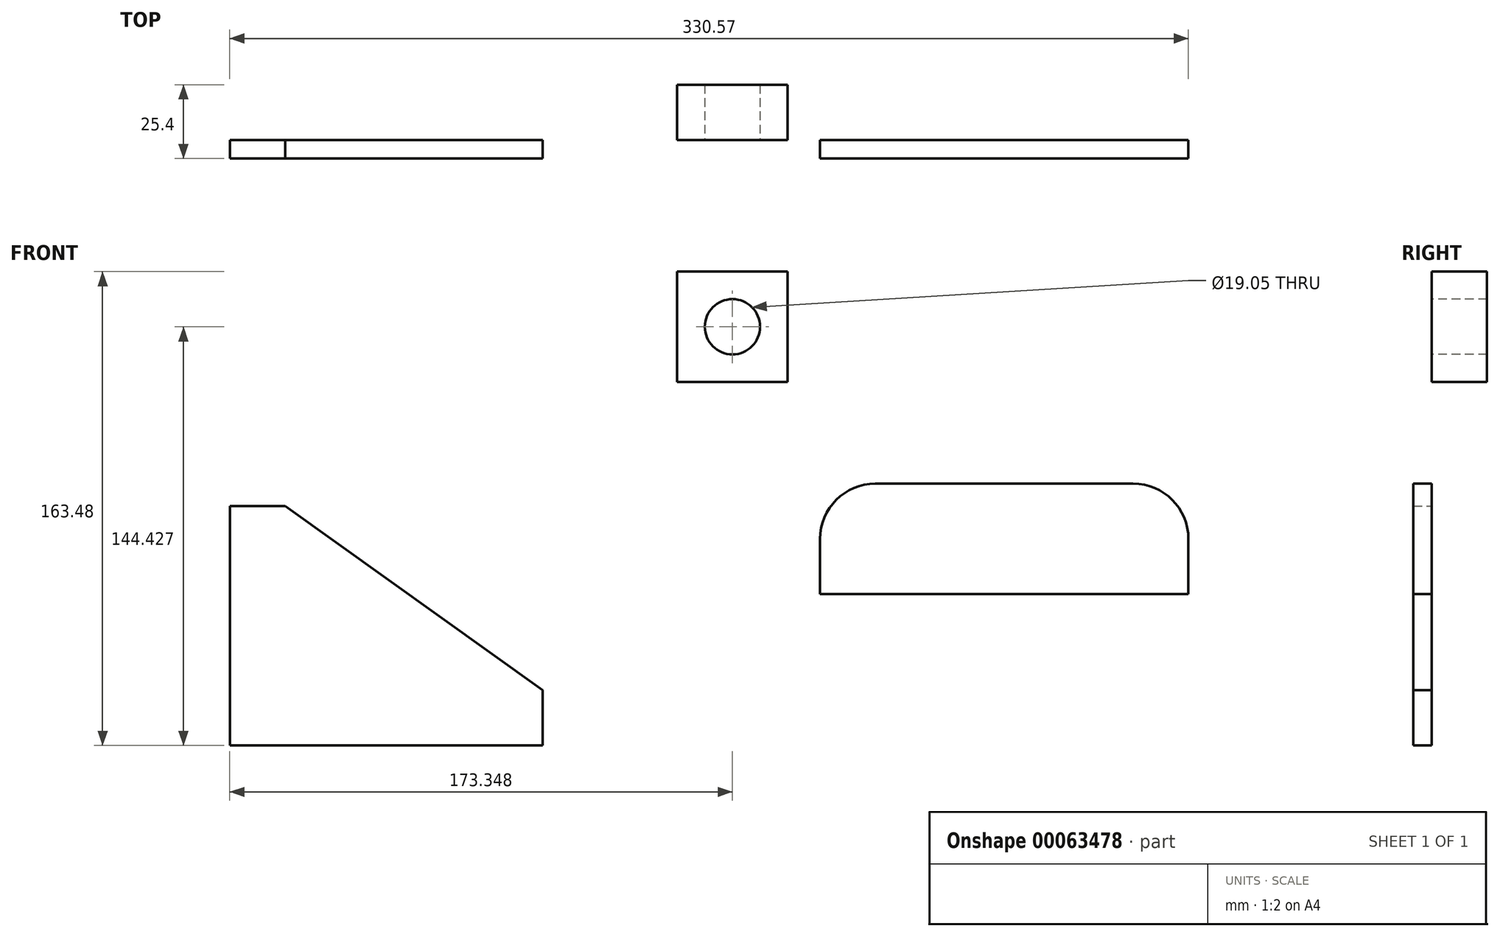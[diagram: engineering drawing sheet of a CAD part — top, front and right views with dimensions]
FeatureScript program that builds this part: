
annotation { "Feature Type Name" : "Feature", "Feature Type Description" : "" }
export const myFeature = defineFeature(function(context is Context, id is Id, definition is map)
    precondition{}
    {
        {
            var Q0;
            Q0=qCreatedBy(makeId("Front.planeOp"),FACE);
            var sketch = newSketch(context, id + "F0", { "sketchPlane" : qUnion([Q0])});
            skLineSegment(sketch, "E0", {"start": v(-40.18, 63.5) * mm, "end": v(-59.23, 63.5) * mm});
            skLineSegment(sketch, "E1", {"start": v(-59.23, 63.5) * mm, "end": v(-59.23, -19.05) * mm});
            skLineSegment(sketch, "E2", {"start": v(-59.23, -19.05) * mm, "end": v(48.72, -19.05) * mm});
            skLineSegment(sketch, "E3", {"start": v(48.72, -19.05) * mm, "end": v(48.72, 0) * mm});
            skLineSegment(sketch, "E4", {"start": v(-40.18, 63.5) * mm, "end": v(48.72, 0) * mm});
            skSolve(sketch);
        }
        {
            var Q0;
            Q0=makeQuery(id+"F0.imprint","IMPRINT",FACE,{"disambiguationData":[TD([[makeQuery(id+"F0.imprint","IMPRINT",EDGE,{"derivedFrom":sQuery(id+"F0.wireOp",EDGE,"E0")}),1.0]])]});
            extrude(context, id + "F1", {"entities" : qUnion([Q0]), "depth" : 6.35 * mm});
        }
        {
            var Q0;
            Q0=qCreatedBy(makeId("Front.planeOp"),FACE);
            var sketch = newSketch(context, id + "F2", { "sketchPlane" : qUnion([Q0])});
            skLineSegment(sketch, "E5.bottom", {"start": v(163.39, 71.27) * mm, "end": v(252.29, 71.27) * mm});
            skLineSegment(sketch, "E5.top", {"start": v(144.34, 33.17) * mm, "end": v(271.34, 33.17) * mm});
            skLineSegment(sketch, "E5.left", {"start": v(144.34, 52.22) * mm, "end": v(144.34, 33.17) * mm});
            skLineSegment(sketch, "E5.right", {"start": v(271.34, 52.22) * mm, "end": v(271.34, 33.17) * mm});
            skPoint(sketch, "E6.visualSharp", {"position": v(144.34, 71.27) * mm});
            skArc(sketch, "E6.filletArc", {"start": v(163.39, 71.27) * mm, "mid": v(149.92, 65.7) * mm, "end": v(144.34, 52.22) * mm});
            skPoint(sketch, "E7.visualSharp", {"position": v(271.34, 71.27) * mm});
            skArc(sketch, "E7.filletArc", {"start": v(271.34, 52.22) * mm, "mid": v(265.76, 65.7) * mm, "end": v(252.29, 71.27) * mm});
            skSolve(sketch);
        }
        {
            var Q0;
            Q0=makeQuery(id+"F2.imprint","IMPRINT",FACE,{"disambiguationData":[TD([[makeQuery(id+"F2.imprint","IMPRINT",EDGE,{"derivedFrom":sQuery(id+"F2.wireOp",EDGE,"E5.bottom")}),-1.0]])]});
            extrude(context, id + "F3", {"entities" : qUnion([Q0]), "depth" : 6.35 * mm});
        }
        {
            var Q0;
            Q0=qCreatedBy(makeId("Front.planeOp"),FACE);
            var sketch = newSketch(context, id + "F4", { "sketchPlane" : qUnion([Q0])});
            skLineSegment(sketch, "E8.bottom", {"start": v(95.07, 106.33) * mm, "end": v(133.17, 106.33) * mm});
            skLineSegment(sketch, "E8.top", {"start": v(95.07, 144.43) * mm, "end": v(133.17, 144.43) * mm});
            skLineSegment(sketch, "E8.left", {"start": v(95.07, 106.33) * mm, "end": v(95.07, 144.43) * mm});
            skLineSegment(sketch, "E8.right", {"start": v(133.17, 106.33) * mm, "end": v(133.17, 144.43) * mm});
            skCircle(sketch, "E9", {"center": v(114.12, 125.38) * mm, "radius": 9.53 * mm});
            skPoint(sketch, "E10.orphan", {"position": v(95.07, 125.38) * mm});
            skPoint(sketch, "E11.end.orphan", {"position": v(133.17, 125.38) * mm});
            skSolve(sketch);
        }
        {
            var Q0;
            Q0=makeQuery(id+"F4.imprint","IMPRINT",FACE,{"disambiguationData":[TD([[makeQuery(id+"F4.imprint","IMPRINT",EDGE,{"derivedFrom":sQuery(id+"F4.wireOp",EDGE,"E8.bottom")}),1.0]])]});
            extrude(context, id + "F5", {"entities" : qUnion([Q0]), "oppositeDirection" : true, "depth" : 19.05 * mm});
        }
    });
